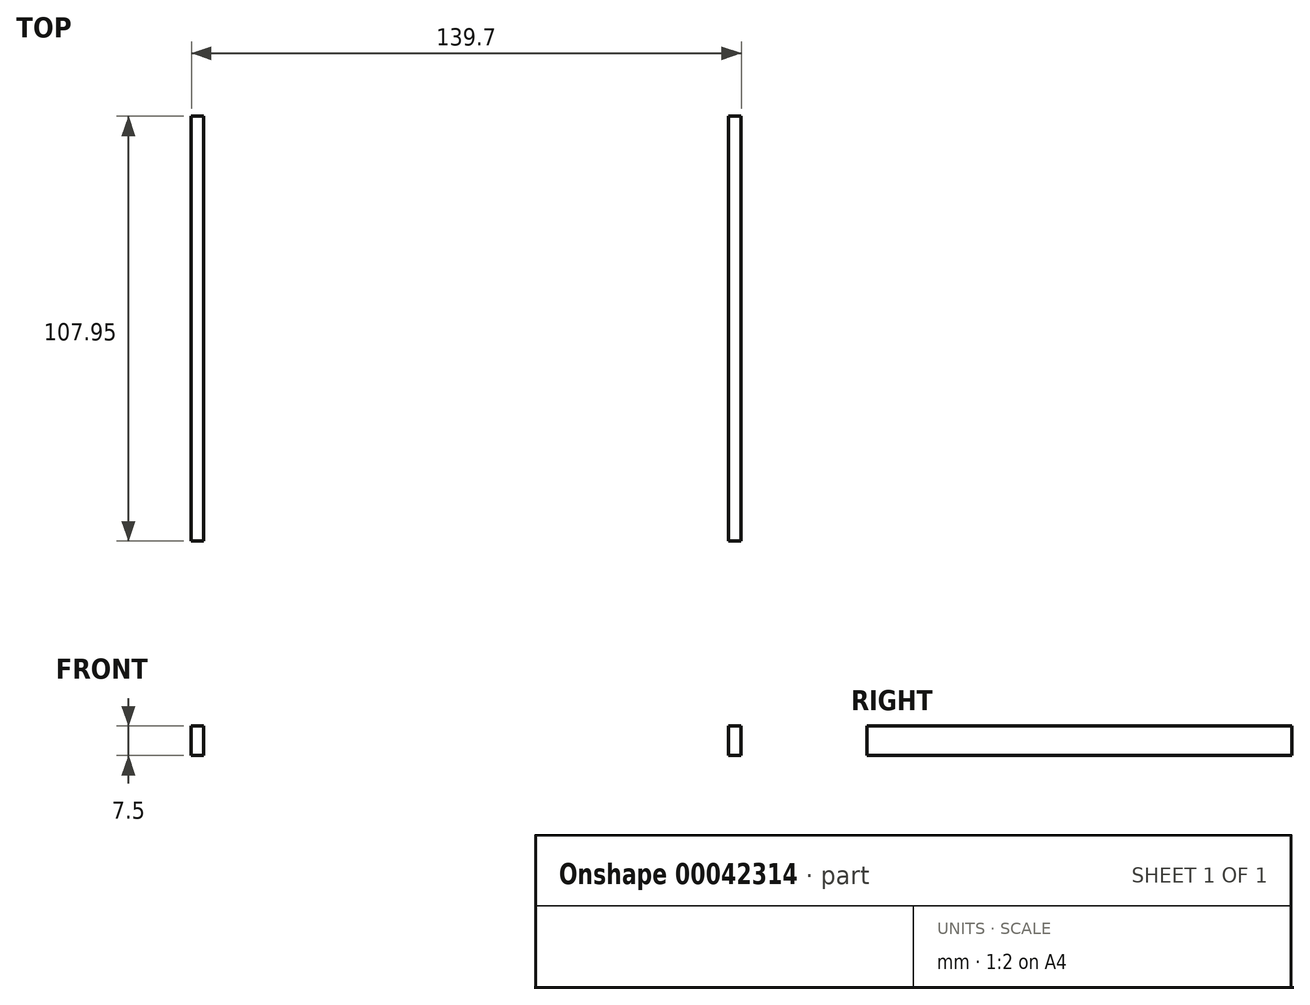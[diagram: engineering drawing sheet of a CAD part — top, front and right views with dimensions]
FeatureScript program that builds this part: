
annotation { "Feature Type Name" : "Feature", "Feature Type Description" : "" }
export const myFeature = defineFeature(function(context is Context, id is Id, definition is map)
    precondition{}
    {
        {
            var Q0;
            Q0=qCreatedBy(makeId("Top.planeOp"),FACE);
            var sketch = newSketch(context, id + "F0", { "sketchPlane" : qUnion([Q0])});
            skLineSegment(sketch, "E0.bottom", {"start": v(-66.1, 56.12) * mm, "end": v(73.6, 56.12) * mm});
            skLineSegment(sketch, "E0.top", {"start": v(-66.1, -51.83) * mm, "end": v(73.6, -51.83) * mm});
            skLineSegment(sketch, "E0.left", {"start": v(-66.1, 56.12) * mm, "end": v(-66.1, -51.83) * mm});
            skLineSegment(sketch, "E0.right", {"start": v(73.6, 56.12) * mm, "end": v(73.6, -51.83) * mm});
            skLineSegment(sketch, "E1", {"start": v(-62.92, 56.12) * mm, "end": v(-62.92, -51.83) * mm});
            skLineSegment(sketch, "E2", {"start": v(70.43, 56.12) * mm, "end": v(70.43, -51.83) * mm});
            skSolve(sketch);
        }
        {
            var Q0;
            {var subQ1=sQuery(id+"F0.wireOp",EDGE,"E0.left");Q0=makeQuery(id+"F0.imprint","IMPRINT",FACE,{"disambiguationData":[TD([[makeQuery(id+"F0.imprint","IMPRINT",EDGE,{"derivedFrom":subQ1}),1.0]])]});}
            var Q1;
            {var subQ1=sQuery(id+"F0.wireOp",EDGE,"E0.right");Q1=makeQuery(id+"F0.imprint","IMPRINT",FACE,{"disambiguationData":[TD([[makeQuery(id+"F0.imprint","IMPRINT",EDGE,{"derivedFrom":subQ1}),-1.0]])]});}
            extrude(context, id + "F1", {"entities" : qUnion([Q0, Q1]), "depth" : 7.5 * mm});
        }
    });
